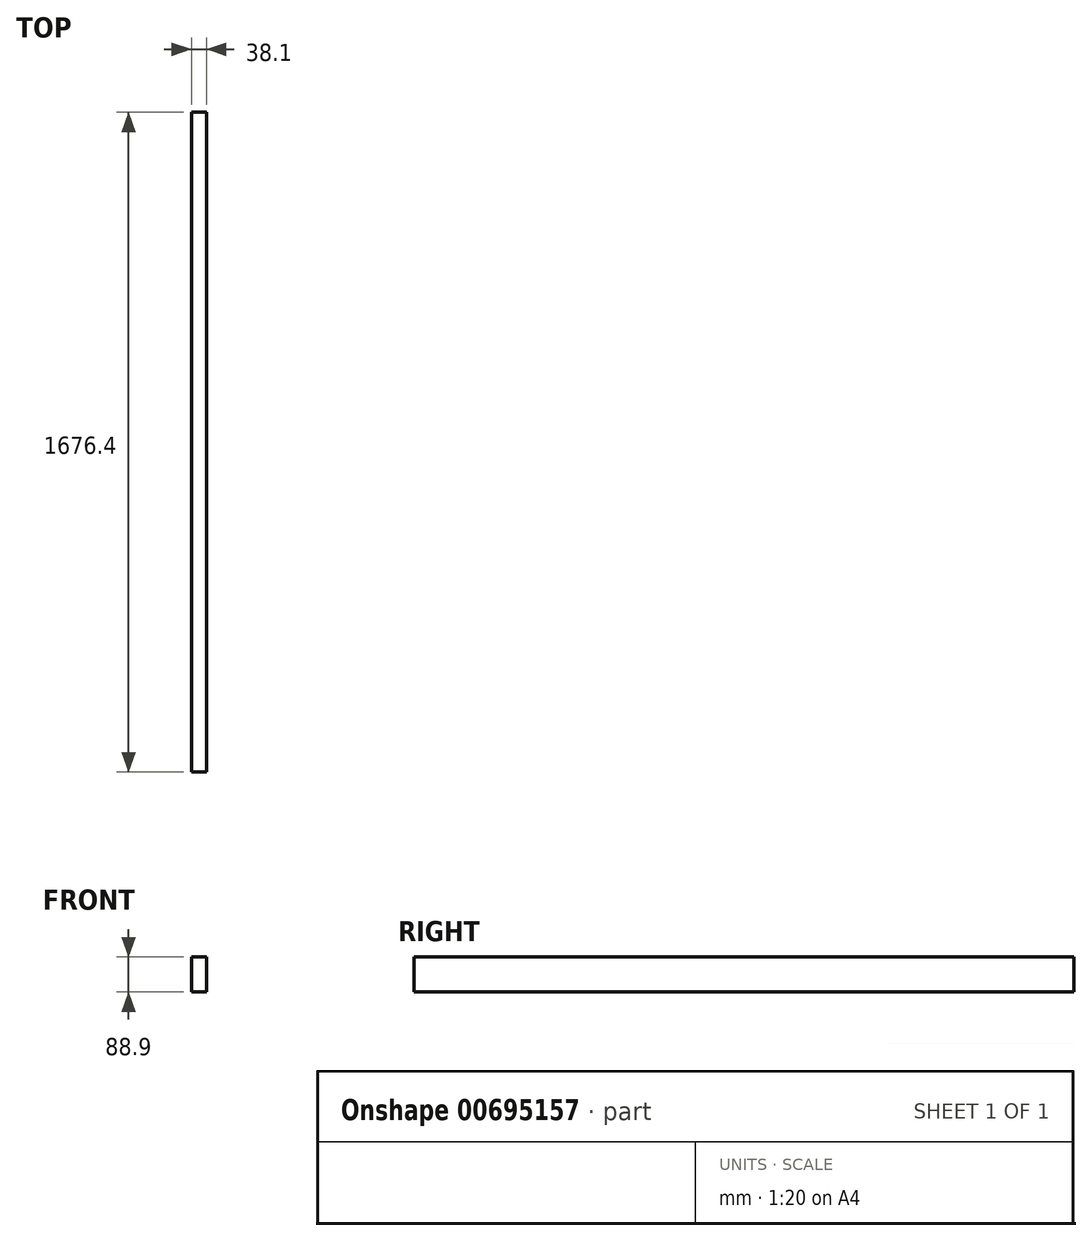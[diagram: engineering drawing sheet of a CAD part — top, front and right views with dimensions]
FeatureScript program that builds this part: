
annotation { "Feature Type Name" : "Feature", "Feature Type Description" : "" }
export const myFeature = defineFeature(function(context is Context, id is Id, definition is map)
    precondition{}
    {
        {
            var Q0;
            Q0=qCreatedBy(makeId("Front.planeOp"),FACE);
            var sketch = newSketch(context, id + "F0", { "sketchPlane" : qUnion([Q0])});
            skLineSegment(sketch, "E0.bottom", {"start": v(227.47, -3.03) * mm, "end": v(265.57, -3.03) * mm});
            skLineSegment(sketch, "E0.top", {"start": v(227.47, -91.93) * mm, "end": v(265.57, -91.93) * mm});
            skLineSegment(sketch, "E0.left", {"start": v(227.47, -3.03) * mm, "end": v(227.47, -91.93) * mm});
            skLineSegment(sketch, "E0.right", {"start": v(265.57, -3.03) * mm, "end": v(265.57, -91.93) * mm});
            skSolve(sketch);
        }
        {
            var Q0;
            Q0=makeQuery(id+"F0.imprint","IMPRINT",FACE,{"disambiguationData":[TD([[makeQuery(id+"F0.imprint","IMPRINT",EDGE,{"derivedFrom":sQuery(id+"F0.wireOp",EDGE,"E0.bottom")}),-1.0]])]});
            extrude(context, id + "F1", {"entities" : qUnion([Q0]), "depth" : 1676.4 * mm, "offsetDistance" : 25.4 * mm});
        }
    });
